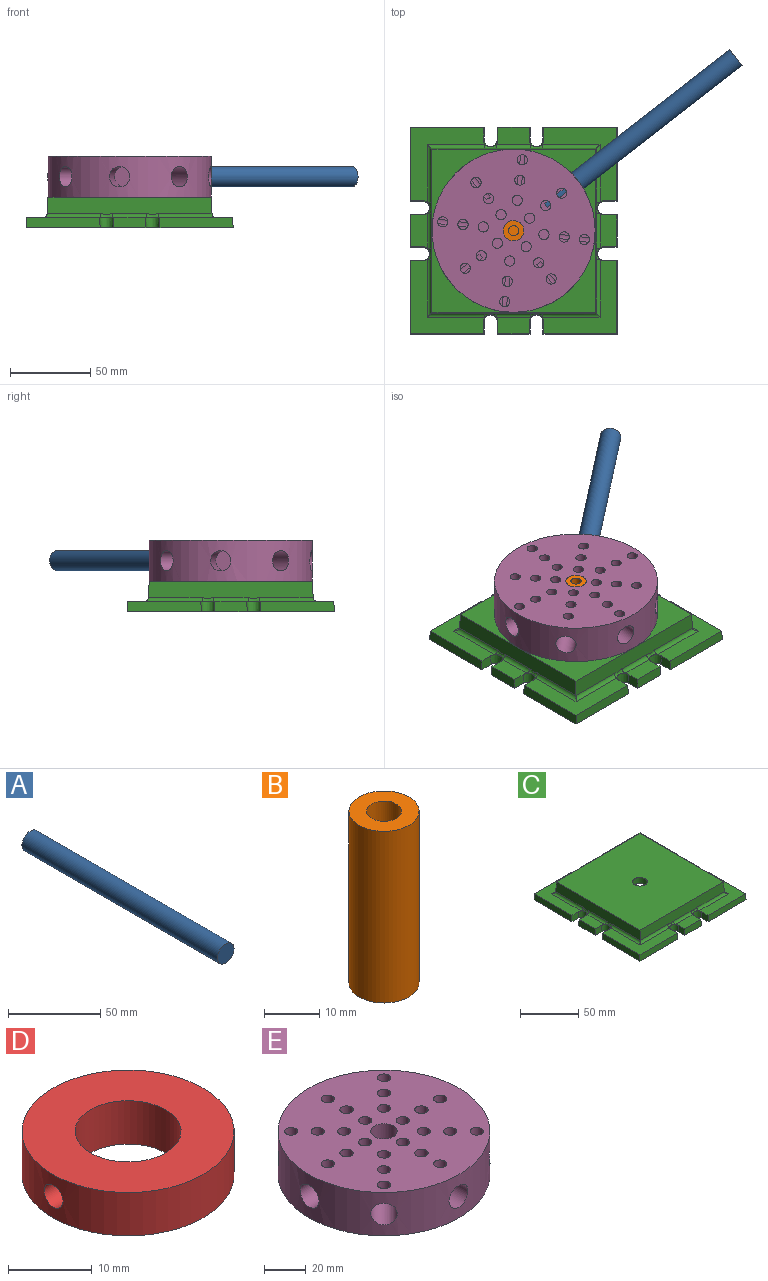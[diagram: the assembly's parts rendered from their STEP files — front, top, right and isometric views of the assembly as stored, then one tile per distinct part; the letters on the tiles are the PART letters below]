
ASSEMBLY  parts=5 mates=4
PART A: 3 faces, bbox 12.7x150x12.7 mm
  f0: cylinder r=6.35mm len=150mm, axis (0,1,0), area 5984.7mm2, adj f1,f2
  f1: plane 12.7x12.7mm, normal (0,-1,0), area 126.7mm2, adj f0
  f2: plane 12.7x12.7mm, normal (0,1,0), area 126.7mm2, adj f0
PART B: 5 faces, bbox 12.7x12.7x38.1 mm
  f0: cylinder r=6.35mm len=38.1mm, axis (0,0,1), area 1520.1mm2, adj f1,f2
  f1: plane 12.7x12.7mm, normal (0,0,-1), area 126.7mm2, adj f0
  f2: plane 12.7x12.7mm, normal (0,0,1), area 95mm2, adj f0,f3
  f3: cylinder r=3.17mm len=12.7mm, axis (0,0,1), area 253.4mm2, adj f2,f4
  f4: plane 6.35x6.35mm, normal (0,0,1), area 31.7mm2, adj f3
PART C: 76 faces, bbox 129x129x19.1 mm
  f0: plane 21.55x10.33mm, normal (0,0,1), area 206.2mm2, adj f12,f44,f45,f47,f48,f72
  f1: plane 46.37x46.37mm, normal (0,0,1), area 834.6mm2, adj f29,f30,f42,f43,f44,f46,f66,f68
  f2: plane 21.55x10.33mm, normal (0,0,1), area 206.2mm2, adj f13,f38,f39,f41,f42,f62
  f3: plane 46.37x46.37mm, normal (0,0,1), area 834.6mm2, adj f14,f31,f36,f37,f38,f40,f56,f58
  f4: plane 21.55x10.33mm, normal (0,0,1), area 206.2mm2, adj f15,f32,f33,f35,f36,f59
  f5: plane 46.37x46.37mm, normal (0,0,1), area 834.6mm2, adj f7,f16,f32,f34,f54,f55,f63,f65
  f6: plane 21.55x10.33mm, normal (0,0,1), area 206.2mm2, adj f8,f50,f51,f53,f54,f69
  f7: plane 46.17x6.35mm, normal (0,1,0.05), area 291.4mm2, adj f5,f9,f16,f55
  f8: plane 20.49x6.35mm, normal (0,1,0.05), area 128.2mm2, adj f6,f9,f51,f53
  f9: plane 129x129mm, normal (0,0,-1), area 8010.8mm2, adj f7,f8,f11,f12,f13,f14,f15,f16
  f10: plane 46.37x46.37mm, normal (0,0,1), area 834.6mm2, adj f11,f28,f48,f49,f50,f52,f73,f75
  f11: plane 46.17x6.35mm, normal (1,0,0.05), area 291.4mm2, adj f9,f10,f28,f49
  f12: plane 20.49x6.35mm, normal (1,0,0.05), area 128.2mm2, adj f0,f9,f45,f47
  f13: plane 20.49x6.35mm, normal (0,-1,0.05), area 128.2mm2, adj f2,f9,f39,f41
  f14: plane 46.17x6.35mm, normal (0,-1,0.05), area 291.4mm2, adj f3,f9,f31,f40
  f15: plane 20.49x6.35mm, normal (-1,0,0.05), area 128.2mm2, adj f4,f9,f33,f35
  f16: plane 46.17x6.35mm, normal (-1,0,0.05), area 291.4mm2, adj f5,f7,f9,f34
  f17: plane 102.68x11.1mm, normal (-1,0,0.05), area 1061.7mm2, adj f18,f20,f23,f56,f57,f59,f61,f63
  f18: plane 102.68x11.1mm, normal (0,-1,0.05), area 1061.7mm2, adj f17,f19,f23,f58,f60,f62,f64,f66
  f19: plane 102.68x11.1mm, normal (1,0,0.05), area 1061.7mm2, adj f18,f20,f23,f68,f70,f72,f74,f75
  f20: plane 102.68x11.1mm, normal (0,1,0.05), area 1061.7mm2, adj f17,f19,f23,f65,f67,f69,f71,f73
  f21: cylinder r=6.35mm len=12.7mm, axis (0,0,1), area 253.4mm2, adj f22,f23
  f22: plane 88.9x88.9mm, normal (0,0,-1), area 7776.5mm2, adj f21,f24,f25,f26,f27
  f23: plane 101.6x101.6mm, normal (0,0,1), area 10195.9mm2, adj f17,f18,f19,f20,f21
  f24: plane 88.9x12.7mm, normal (0,-1,0), area 1129mm2, adj f9,f22,f25,f27
  f25: plane 88.9x12.7mm, normal (1,0,0), area 1129mm2, adj f9,f22,f24,f26
  f26: plane 88.9x12.7mm, normal (0,1,0), area 1129mm2, adj f9,f22,f25,f27
  f27: plane 88.9x12.7mm, normal (-1,0,0), area 1129mm2, adj f9,f22,f24,f26
  f28: plane 46.17x6.35mm, normal (0,1,0.05), area 291.4mm2, adj f9,f10,f11,f52
  f29: plane 46.17x6.35mm, normal (1,0,0.05), area 291.4mm2, adj f1,f9,f30,f46
  f30: plane 46.17x6.35mm, normal (0,-1,0.05), area 291.4mm2, adj f1,f9,f29,f43
  f31: plane 46.17x6.35mm, normal (-1,0,0.05), area 291.4mm2, adj f3,f9,f14,f37
  f32: cone r=5.04mm half-angle=3deg, axis (0,0,1), area 84.1mm2, adj f4,f5,f9,f33,f34,f61
  f33: plane 8.05x6.35mm, normal (0,1,0.05), area 50.1mm2, adj f4,f9,f15,f32
  f34: plane 8.05x6.35mm, normal (0,-1,0.05), area 50.1mm2, adj f5,f9,f16,f32
  f35: plane 8.05x6.35mm, normal (0,-1,0.05), area 50.1mm2, adj f4,f9,f15,f36
  f36: cone r=5.04mm half-angle=3deg, axis (0,0,1), area 84.1mm2, adj f3,f4,f9,f35,f37,f57
  f37: plane 8.05x6.35mm, normal (0,1,0.05), area 50.1mm2, adj f3,f9,f31,f36
  f38: cone r=5.04mm half-angle=3deg, axis (0,0,1), area 84.1mm2, adj f2,f3,f9,f39,f40,f60
  f39: plane 8.05x6.35mm, normal (-1,0,0.05), area 50.1mm2, adj f2,f9,f13,f38
  f40: plane 8.05x6.35mm, normal (1,0,0.05), area 50.1mm2, adj f3,f9,f14,f38
  f41: plane 8.05x6.35mm, normal (1,0,0.05), area 50.1mm2, adj f2,f9,f13,f42
  f42: cone r=5.04mm half-angle=3deg, axis (0,0,1), area 84.1mm2, adj f1,f2,f9,f41,f43,f64
  f43: plane 8.05x6.35mm, normal (-1,0,0.05), area 50.1mm2, adj f1,f9,f30,f42
  f44: cone r=5.04mm half-angle=3deg, axis (0,0,1), area 84.1mm2, adj f0,f1,f9,f45,f46,f70
  f45: plane 8.05x6.35mm, normal (0,-1,0.05), area 50.1mm2, adj f0,f9,f12,f44
  f46: plane 8.05x6.35mm, normal (0,1,0.05), area 50.1mm2, adj f1,f9,f29,f44
  f47: plane 8.05x6.35mm, normal (0,1,0.05), area 50.1mm2, adj f0,f9,f12,f48
  f48: cone r=5.04mm half-angle=3deg, axis (0,0,1), area 84.1mm2, adj f0,f9,f10,f47,f49,f74
  f49: plane 8.05x6.35mm, normal (0,-1,0.05), area 50.1mm2, adj f9,f10,f11,f48
  f50: cone r=5.04mm half-angle=3deg, axis (0,0,1), area 84.1mm2, adj f6,f9,f10,f51,f52,f71
  f51: plane 8.05x6.35mm, normal (1,0,0.05), area 50.1mm2, adj f6,f8,f9,f50
  f52: plane 8.05x6.35mm, normal (-1,0,0.05), area 50.1mm2, adj f9,f10,f28,f50
  f53: plane 8.05x6.35mm, normal (-1,0,0.05), area 50.1mm2, adj f6,f8,f9,f54
  f54: cone r=5.04mm half-angle=3deg, axis (0,0,1), area 84.1mm2, adj f5,f6,f9,f53,f55,f67
  f55: plane 8.05x6.35mm, normal (1,0,0.05), area 50.1mm2, adj f5,f7,f9,f54
  f56: cylinder r=2.5mm len=36.04mm, axis (0,-1,0), area 130.9mm2, adj f3,f17,f57,f58
  f57: bspline ~7.96x2.76mm, area 17.7mm2, adj f17,f36,f56,f59
  f58: cylinder r=2.5mm len=36.04mm, axis (1,0,0), area 130.9mm2, adj f3,f18,f56,f60
  f59: cylinder r=2.5mm len=21.55mm, axis (0,-1,0), area 81.8mm2, adj f4,f17,f57,f61
  f60: bspline ~7.96x2.76mm, area 17.7mm2, adj f18,f38,f58,f62
  f61: bspline ~7.96x2.76mm, area 17.7mm2, adj f17,f32,f59,f63
  f62: cylinder r=2.5mm len=21.55mm, axis (1,0,0), area 81.8mm2, adj f2,f18,f60,f64
  f63: cylinder r=2.5mm len=36.04mm, axis (0,-1,0), area 130.9mm2, adj f5,f17,f61,f65
  f64: bspline ~7.96x2.76mm, area 17.7mm2, adj f18,f42,f62,f66
  f65: cylinder r=2.5mm len=36.04mm, axis (1,0,0), area 130.9mm2, adj f5,f20,f63,f67
  f66: cylinder r=2.5mm len=36.04mm, axis (1,0,0), area 130.9mm2, adj f1,f18,f64,f68
  f67: bspline ~7.96x2.76mm, area 17.7mm2, adj f20,f54,f65,f69
  f68: cylinder r=2.5mm len=36.04mm, axis (0,-1,0), area 130.9mm2, adj f1,f19,f66,f70
  f69: cylinder r=2.5mm len=21.55mm, axis (1,0,0), area 81.8mm2, adj f6,f20,f67,f71
  f70: bspline ~7.96x2.76mm, area 17.7mm2, adj f19,f44,f68,f72
  f71: bspline ~7.96x2.76mm, area 17.7mm2, adj f20,f50,f69,f73
  f72: cylinder r=2.5mm len=21.55mm, axis (0,-1,0), area 81.8mm2, adj f0,f19,f70,f74
  f73: cylinder r=2.5mm len=36.04mm, axis (1,0,0), area 130.9mm2, adj f10,f20,f71,f75
  f74: bspline ~7.96x2.76mm, area 17.7mm2, adj f19,f48,f72,f75
  f75: cylinder r=2.5mm len=36.04mm, axis (0,-1,0), area 130.9mm2, adj f10,f19,f73,f74
PART D: 5 faces, bbox 25.4x25.4x6.4 mm
  f0: cylinder r=6.35mm len=12.7mm, axis (0,0,-1), area 245.4mm2, adj f2,f3,f4
  f1: cylinder r=12.7mm len=25.4mm, axis (0,0,-1), area 498.7mm2, adj f2,f3,f4
  f2: plane 25.4x25.4mm, normal (0,0,1), area 380mm2, adj f0,f1
  f3: plane 25.4x25.4mm, normal (0,0,-1), area 380mm2, adj f0,f1
  f4: cylinder r=1.59mm len=6.55mm, axis (-1,0,0), area 63.8mm2, adj f0,f1
PART E: 80 faces, bbox 101.6x101.6x25.4 mm
  f0: plane 101.6x101.6mm, normal (0,0,1), area 7220.6mm2, adj f17,f19,f21,f24,f27,f30,f32,f35
  f1: cylinder r=6.35mm len=25.4mm, axis (-1,0,0), area 980mm2, adj f10,f41,f42,f43,f44,f45,f79
  f2: cylinder r=6.35mm len=25.4mm, axis (0,1,0), area 980mm2, adj f11,f30,f31,f32,f33,f34,f79
  f3: cylinder r=6.35mm len=26.94mm, axis (-0.71,0.71,0), area 971.5mm2, adj f15,f35,f36,f37,f38,f39,f40,f79
  f4: cylinder r=6.35mm len=25.4mm, axis (0,-1,0), area 980mm2, adj f9,f52,f53,f54,f55,f56,f79
  f5: cylinder r=6.35mm len=25.4mm, axis (1,0,0), area 980mm2, adj f12,f19,f20,f21,f22,f23,f79
  f6: cylinder r=6.35mm len=26.94mm, axis (0.71,-0.71,0), area 971.5mm2, adj f13,f57,f58,f59,f60,f61,f62,f79
  f7: cylinder r=6.35mm len=26.94mm, axis (-0.71,-0.71,0), area 971.5mm2, adj f14,f46,f47,f48,f49,f50,f51,f79
  f8: cylinder r=6.35mm len=26.94mm, axis (0.71,0.71,0), area 971.5mm2, adj f16,f24,f25,f26,f27,f28,f29,f79
  f9: plane 12.7x12.55mm, normal (0,-1,0), area 126.4mm2, adj f4,f53
  f10: plane 12.7x12.55mm, normal (-1,0,0), area 126.4mm2, adj f1,f42
  f11: plane 12.7x12.55mm, normal (0,1,0), area 126.4mm2, adj f2,f31
  f12: plane 12.7x12.55mm, normal (1,0,0), area 126.4mm2, adj f5,f20
  f13: plane 12.7x8.98mm, normal (0.71,-0.71,0), area 126.7mm2, adj f6
  f14: plane 12.7x8.98mm, normal (-0.71,-0.71,0), area 126.7mm2, adj f7
  f15: plane 12.7x8.98mm, normal (-0.71,0.71,0), area 126.7mm2, adj f3
  f16: plane 12.7x8.98mm, normal (0.71,0.71,0), area 126.7mm2, adj f8
  f17: cylinder r=6.35mm len=25.4mm, axis (0,0,-1), area 1013.4mm2, adj f0,f18
  f18: plane 101.6x101.6mm, normal (0,0,-1), area 7980.6mm2, adj f17,f79
  f19: cylinder r=3.17mm len=6.5mm, axis (0,0,1), area 129.4mm2, adj f0,f5,f20
  f20: plane 6.35x6.04mm, normal (0,0,1), area 23.2mm2, adj f5,f12,f19
  f21: cylinder r=3.17mm len=6.5mm, axis (0,0,1), area 129.1mm2, adj f0,f5,f22,f23
  f22: plane 5.73x1.8mm, normal (0,0,1), area 7.4mm2, adj f5,f21
  f23: plane 5.73x1.8mm, normal (0,0,1), area 7.4mm2, adj f5,f21
  f24: cylinder r=3.17mm len=6.5mm, axis (0,0,1), area 129.1mm2, adj f0,f8,f25,f26
  f25: plane 4.23x4.23mm, normal (0,0,1), area 7.4mm2, adj f8,f24
  f26: plane 4.23x4.23mm, normal (0,0,1), area 7.4mm2, adj f8,f24
  f27: cylinder r=3.17mm len=6.5mm, axis (0,0,1), area 129.1mm2, adj f0,f8,f28,f29
  f28: plane 4.23x4.23mm, normal (0,0,1), area 7.4mm2, adj f8,f27
  f29: plane 4.23x4.23mm, normal (0,0,1), area 7.4mm2, adj f8,f27
  f30: cylinder r=3.17mm len=6.5mm, axis (0,0,1), area 129.4mm2, adj f0,f2,f31
  f31: plane 6.35x6.04mm, normal (0,0,1), area 23.2mm2, adj f2,f11,f30
  f32: cylinder r=3.17mm len=6.5mm, axis (0,0,1), area 129.1mm2, adj f0,f2,f33,f34
  f33: plane 5.73x1.8mm, normal (0,0,1), area 7.4mm2, adj f2,f32
  f34: plane 5.73x1.8mm, normal (0,0,1), area 7.4mm2, adj f2,f32
  f35: cylinder r=3.17mm len=6.5mm, axis (0,0,1), area 129.1mm2, adj f0,f3,f36,f37
  f36: plane 4.23x4.23mm, normal (0,0,1), area 7.4mm2, adj f3,f35
  f37: plane 4.23x4.23mm, normal (0,0,1), area 7.4mm2, adj f3,f35
  f38: cylinder r=3.17mm len=6.5mm, axis (0,0,1), area 129.1mm2, adj f0,f3,f39,f40
  f39: plane 4.23x4.23mm, normal (0,0,1), area 7.4mm2, adj f3,f38
  f40: plane 4.23x4.23mm, normal (0,0,1), area 7.4mm2, adj f3,f38
  f41: cylinder r=3.17mm len=6.5mm, axis (0,0,1), area 129.4mm2, adj f0,f1,f42
  f42: plane 6.35x6.04mm, normal (0,0,1), area 23.2mm2, adj f1,f10,f41
  f43: cylinder r=3.17mm len=6.5mm, axis (0,0,1), area 129.1mm2, adj f0,f1,f44,f45
  f44: plane 5.73x1.8mm, normal (0,0,1), area 7.4mm2, adj f1,f43
  f45: plane 5.73x1.8mm, normal (0,0,1), area 7.4mm2, adj f1,f43
  f46: cylinder r=3.17mm len=6.5mm, axis (0,0,1), area 129.1mm2, adj f0,f7,f47,f48
  f47: plane 4.23x4.23mm, normal (0,0,1), area 7.4mm2, adj f7,f46
  f48: plane 4.23x4.23mm, normal (0,0,1), area 7.4mm2, adj f7,f46
  f49: cylinder r=3.17mm len=6.5mm, axis (0,0,1), area 129.1mm2, adj f0,f7,f50,f51
  f50: plane 4.23x4.23mm, normal (0,0,1), area 7.4mm2, adj f7,f49
  f51: plane 4.23x4.23mm, normal (0,0,1), area 7.4mm2, adj f7,f49
  f52: cylinder r=3.17mm len=6.5mm, axis (0,0,1), area 129.4mm2, adj f0,f4,f53
  f53: plane 6.35x6.04mm, normal (0,0,1), area 23.2mm2, adj f4,f9,f52
  f54: cylinder r=3.17mm len=6.5mm, axis (0,0,1), area 129.1mm2, adj f0,f4,f55,f56
  f55: plane 5.73x1.8mm, normal (0,0,1), area 7.4mm2, adj f4,f54
  f56: plane 5.73x1.8mm, normal (0,0,1), area 7.4mm2, adj f4,f54
  f57: cylinder r=3.17mm len=6.5mm, axis (0,0,1), area 129.1mm2, adj f0,f6,f58,f59
  f58: plane 4.23x4.23mm, normal (0,0,1), area 7.4mm2, adj f6,f57
  f59: plane 4.23x4.23mm, normal (0,0,1), area 7.4mm2, adj f6,f57
  f60: cylinder r=3.17mm len=6.5mm, axis (0,0,1), area 129.1mm2, adj f0,f6,f61,f62
  f61: plane 4.23x4.23mm, normal (0,0,1), area 7.4mm2, adj f6,f60
  f62: plane 4.23x4.23mm, normal (0,0,1), area 7.4mm2, adj f6,f60
  f63: cylinder r=3.17mm len=6.5mm, axis (0,0,1), area 129.7mm2, adj f0,f64
  f64: plane 6.35x6.35mm, normal (0,0,1), area 31.7mm2, adj f63
  f65: cylinder r=3.17mm len=6.5mm, axis (0,0,1), area 129.7mm2, adj f0,f66
  f66: plane 6.35x6.35mm, normal (0,0,1), area 31.7mm2, adj f65
  f67: cylinder r=3.17mm len=6.5mm, axis (0,0,1), area 129.7mm2, adj f0,f68
  f68: plane 6.35x6.35mm, normal (0,0,1), area 31.7mm2, adj f67
  f69: cylinder r=3.17mm len=6.5mm, axis (0,0,1), area 129.7mm2, adj f0,f70
  f70: plane 6.35x6.35mm, normal (0,0,1), area 31.7mm2, adj f69
  f71: cylinder r=3.17mm len=6.5mm, axis (0,0,1), area 129.7mm2, adj f0,f72
  f72: plane 6.35x6.35mm, normal (0,0,1), area 31.7mm2, adj f71
  f73: cylinder r=3.17mm len=6.5mm, axis (0,0,1), area 129.7mm2, adj f0,f74
  f74: plane 6.35x6.35mm, normal (0,0,1), area 31.7mm2, adj f73
  f75: cylinder r=3.17mm len=6.5mm, axis (0,0,1), area 129.7mm2, adj f0,f76
  f76: plane 6.35x6.35mm, normal (0,0,1), area 31.7mm2, adj f75
  f77: cylinder r=3.17mm len=6.5mm, axis (0,0,1), area 129.7mm2, adj f0,f78
  f78: plane 6.35x6.35mm, normal (0,0,1), area 31.7mm2, adj f77
  f79: cylinder r=50.8mm len=101.6mm, axis (0,0,1), area 7092.5mm2, adj f0,f1,f2,f3,f4,f5,f6,f7
PLACE A rot(axis=(0,0,1),127.9deg) t=(-120.12,-37.6,43.57)mm
PLACE B rot(axis=(0,0,1),127.9deg) t=(-120.12,-37.6,43.57)mm
PLACE C t=(-120.12,-37.6,43.57)mm fixed
PLACE D rot(axis=(0,0,1),127.9deg) t=(-120.12,-37.6,43.57)mm
PLACE E rot(axis=(0,0,1),127.9deg) t=(-120.12,-37.6,43.57)mm
MATE revolute C.f21 <-> B.f0  axis (0,0,1) through (-120.12,-37.6,43.57)mm
MATE fastened A.f0 <-> E.f4  axis (-0.79,-0.61,0) through (-100.08,-21.99,56.27)mm
MATE fastened D.f0 <-> B.f0  axis (0,0,-1) through (-120.12,-37.6,30.87)mm
MATE fastened E.f17 <-> B.f0  axis (0,0,1) through (-120.12,-37.6,68.97)mm
